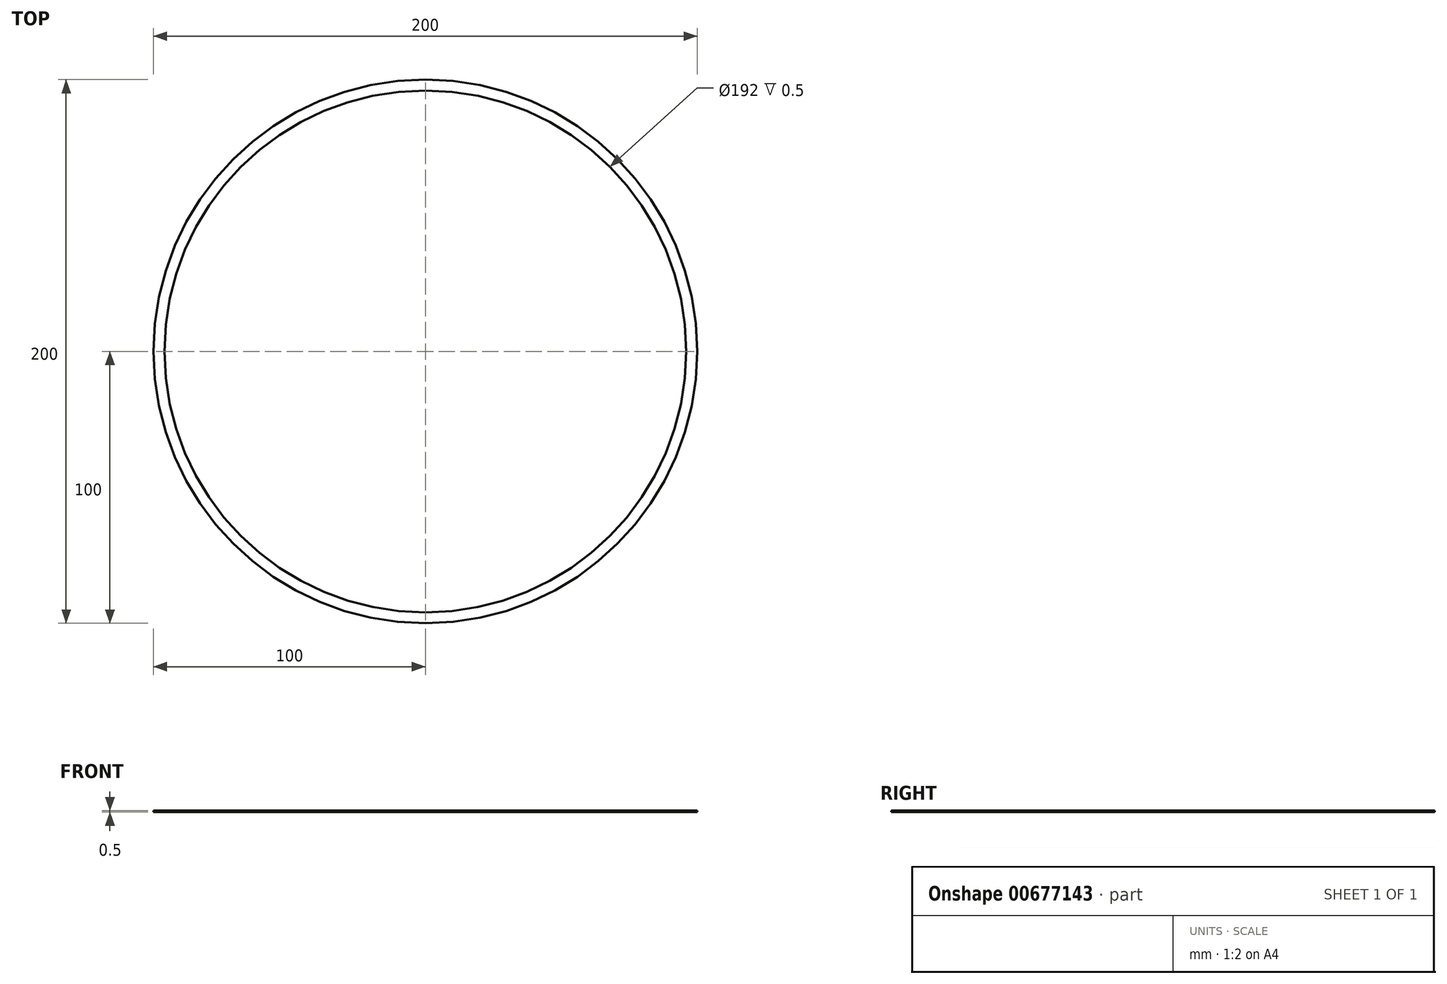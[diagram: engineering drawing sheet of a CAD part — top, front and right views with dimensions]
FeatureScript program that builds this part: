
annotation { "Feature Type Name" : "Feature", "Feature Type Description" : "" }
export const myFeature = defineFeature(function(context is Context, id is Id, definition is map)
    precondition{}
    {
        {
            var Q0;
            Q0=qCreatedBy(makeId("Top.planeOp"),FACE);
            var sketch = newSketch(context, id + "F0", { "sketchPlane" : qUnion([Q0])});
            skCircle(sketch, "E0", {"center": v(0, 0) * mm, "radius": 100 * mm});
            skCircle(sketch, "E1", {"center": v(0, 0) * mm, "radius": 96 * mm});
            skSolve(sketch);
        }
        {
            var Q0;
            Q0=makeQuery(id+"F0.imprint","IMPRINT",FACE,{"disambiguationData":[TD([[makeQuery(id+"F0.imprint","IMPRINT",EDGE,{"derivedFrom":sQuery(id+"F0.wireOp",EDGE,"E0")}),1.0]])]});
            extrude(context, id + "F1", {"entities" : qUnion([Q0]), "depth" : .5 * mm, "offsetDistance" : 25 * mm});
        }
    });
